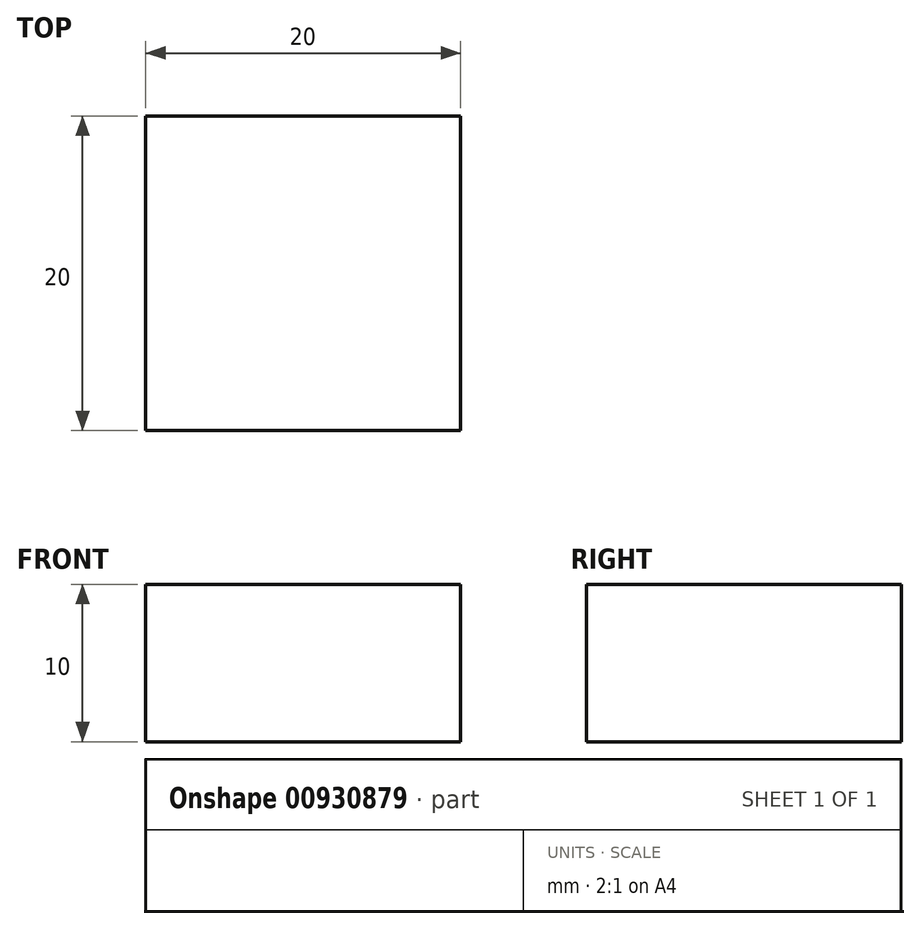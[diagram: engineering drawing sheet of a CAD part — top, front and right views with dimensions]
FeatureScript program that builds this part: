
annotation { "Feature Type Name" : "Feature", "Feature Type Description" : "" }
export const myFeature = defineFeature(function(context is Context, id is Id, definition is map)
    precondition{}
    {
        {
            var Q0;
            Q0=qCreatedBy(makeId("Top.planeOp"),FACE);
            var sketch = newSketch(context, id + "F0", { "sketchPlane" : qUnion([Q0])});
            skLineSegment(sketch, "E0.bottom", {"start": v(0, 0) * mm, "end": v(-20, 0) * mm});
            skLineSegment(sketch, "E0.top", {"start": v(0, -20) * mm, "end": v(-20, -20) * mm});
            skLineSegment(sketch, "E0.left", {"start": v(0, 0) * mm, "end": v(0, -20) * mm});
            skLineSegment(sketch, "E0.right", {"start": v(-20, 0) * mm, "end": v(-20, -20) * mm});
            skSolve(sketch);
        }
        {
            var Q0;
            Q0 = qSketchRegion(id + "F0", true);
            extrude(context, id + "F1", {"entities" : qUnion([Q0]), "depth" : 10 * mm, "offsetDistance" : 25 * mm});
        }
    });
